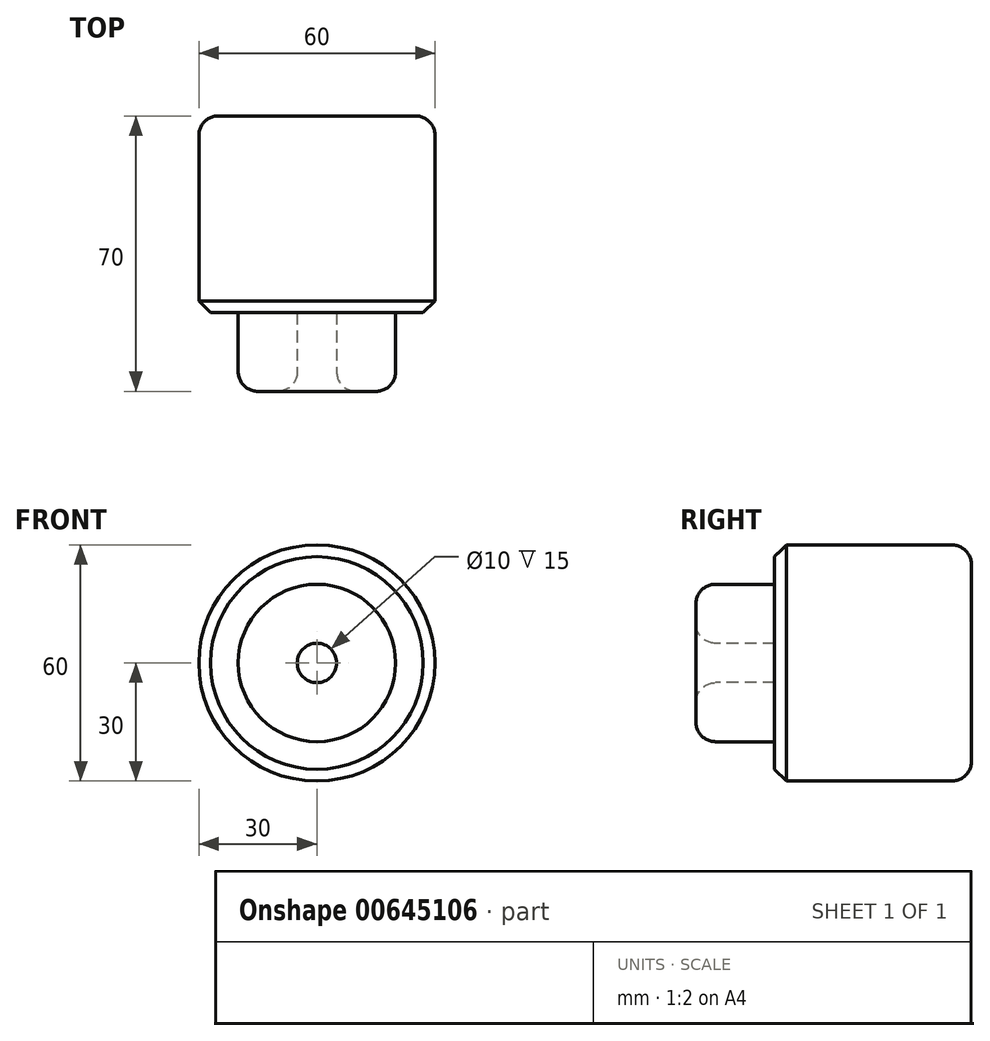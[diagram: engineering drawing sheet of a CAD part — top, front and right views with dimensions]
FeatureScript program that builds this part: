
annotation { "Feature Type Name" : "Feature", "Feature Type Description" : "" }
export const myFeature = defineFeature(function(context is Context, id is Id, definition is map)
    precondition{}
    {
        {
            var Q0;
            Q0=qCreatedBy(makeId("Right.planeOp"),FACE);
            var sketch = newSketch(context, id + "F0", { "sketchPlane" : qUnion([Q0])});
            skLineSegment(sketch, "E0.bottom", {"start": v(-50, 30) * mm, "end": v(0, 30) * mm});
            skLineSegment(sketch, "E0.top", {"start": v(-50, 0) * mm, "end": v(0, 0) * mm});
            skLineSegment(sketch, "E0.left", {"start": v(-50, 30) * mm, "end": v(-50, 0) * mm});
            skLineSegment(sketch, "E0.right", {"start": v(0, 30) * mm, "end": v(0, 0) * mm});
            skLineSegment(sketch, "E1.bottom", {"start": v(-70, 5) * mm, "end": v(-7.04, 5) * mm});
            skLineSegment(sketch, "E1.top", {"start": v(-70, 20) * mm, "end": v(-7.04, 20) * mm});
            skLineSegment(sketch, "E1.left", {"start": v(-70, 5) * mm, "end": v(-70, 20) * mm});
            skLineSegment(sketch, "E1.right", {"start": v(-7.04, 5) * mm, "end": v(-7.04, 20) * mm});
            skSolve(sketch);
        }
        {
            var Q0;
            {var subQ5=sQuery(id+"F0.wireOp",EDGE,"E1.left");Q0=makeQuery(id+"F0.imprint","IMPRINT",FACE,{"disambiguationData":[TD([[makeQuery(id+"F0.imprint","IMPRINT",EDGE,{"derivedFrom":subQ5}),-1.0]])]});}
            var Q1;
            {var subQ4=sQuery(id+"F0.wireOp",EDGE,"E0.bottom");Q1=makeQuery(id+"F0.imprint","IMPRINT",FACE,{"disambiguationData":[TD([[makeQuery(id+"F0.imprint","IMPRINT",EDGE,{"derivedFrom":subQ4}),-1.0]])]});}
            var Q2;
            {var subQ5=sQuery(id+"F0.wireOp",EDGE,"E1.right");Q2=makeQuery(id+"F0.imprint","IMPRINT",FACE,{"disambiguationData":[TD([[makeQuery(id+"F0.imprint","IMPRINT",EDGE,{"derivedFrom":subQ5}),1.0]])]});}
            var Q3;
            Q3=sQuery(id+"F0.wireOp",EDGE,"E0.top");
            revolve(context, id + "F1", {"entities" : qUnion([Q0, Q1, Q2]), "axis" : qUnion([Q3]), "revolveType" : RevolveType.FULL});
        }
        {
            var Q0;
            Q0=makeQuery(id+"F1.opRevolve","SWEPT_EDGE",EDGE,{"disambiguationData":[OSD([sQuery(id+"F0.wireOp",EDGE,"E0.bottom"),sQuery(id+"F0.wireOp",EDGE,"E0.left")])]});
            chamfer(context, id + "F2", {"entities" : qUnion([Q0]), "width" : 3 * mm, "tangentPropagation" : true});
        }
        {
            var Q0;
            Q0=makeQuery(id+"F1.opRevolve","SWEPT_FACE",FACE,{"disambiguationData":[OSD([sQuery(id+"F0.wireOp",EDGE,"E1.left")])]});
            var Q1;
            Q1=makeQuery(id+"F1.opRevolve","SWEPT_EDGE",EDGE,{"disambiguationData":[OSD([sQuery(id+"F0.wireOp",EDGE,"E0.bottom"),sQuery(id+"F0.wireOp",EDGE,"E0.right")])]});
            fillet(context, id + "F3", {"entities" : qUnion([Q0, Q1]), "radius" : 5 * mm, "tangentPropagation" : true, "allowEdgeOverflow" : false});
        }
    });
